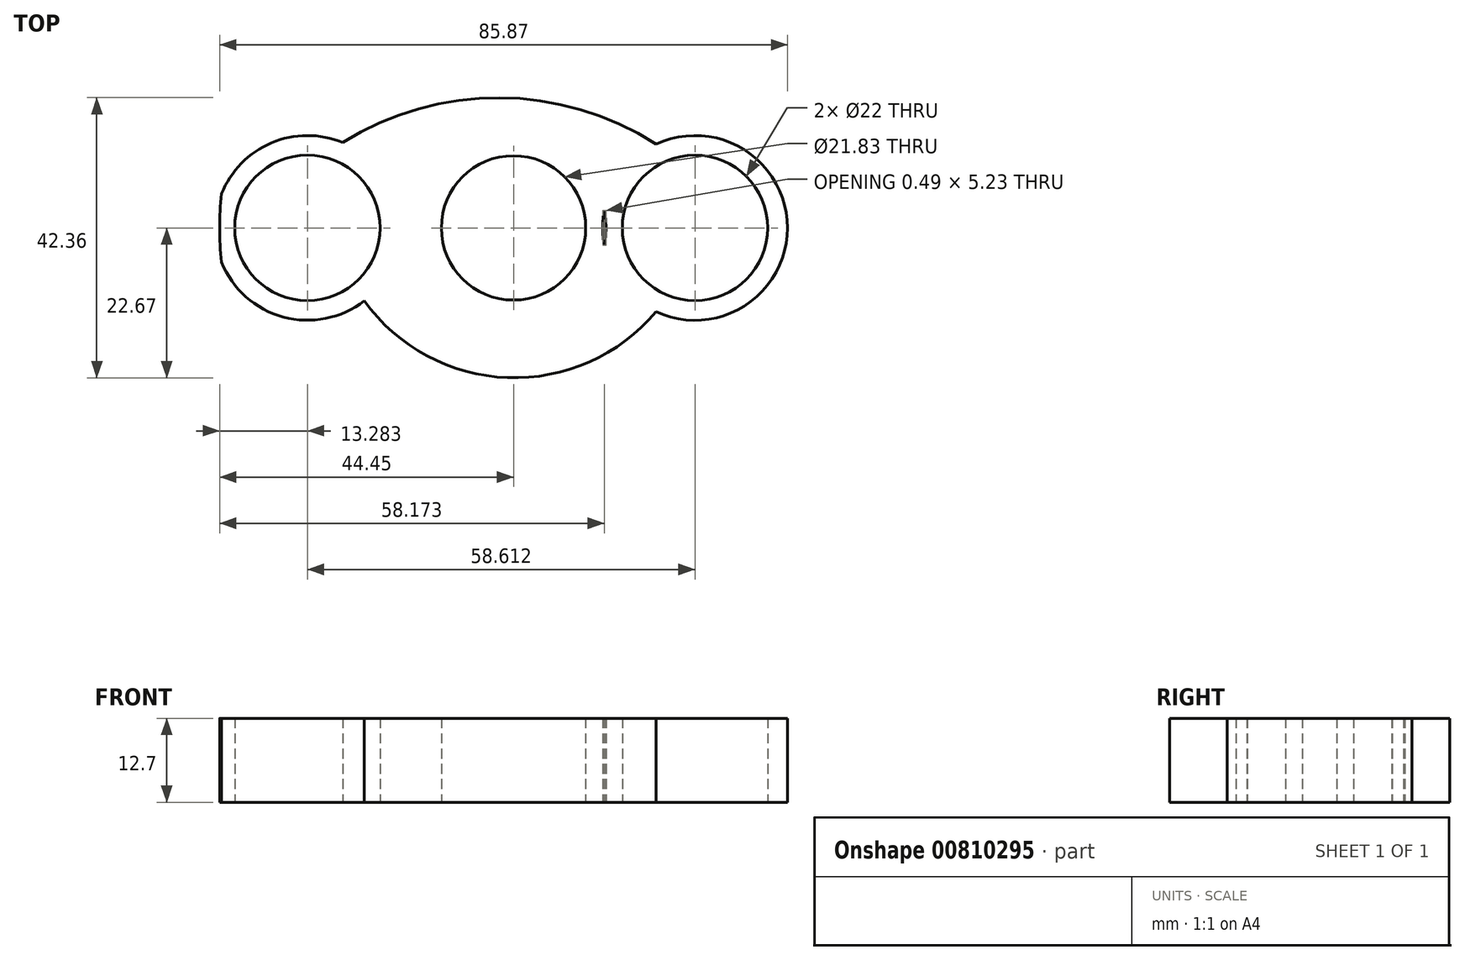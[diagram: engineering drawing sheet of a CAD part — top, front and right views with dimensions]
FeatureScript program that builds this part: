
annotation { "Feature Type Name" : "Feature", "Feature Type Description" : "" }
export const myFeature = defineFeature(function(context is Context, id is Id, definition is map)
    precondition{}
    {
        {
            var Q0;
            Q0=qCreatedBy(makeId("Top.planeOp"),FACE);
            var sketch = newSketch(context, id + "F0", { "sketchPlane" : qUnion([Q0])});
            skCircle(sketch, "E0", {"center": v(0, 0) * mm, "radius": 44.45 * mm});
            skCircle(sketch, "E1", {"center": v(0, 0) * mm, "radius": 10.91 * mm});
            skCircle(sketch, "E2", {"center": v(-31.17, 0) * mm, "radius": 11 * mm});
            skCircle(sketch, "E3", {"center": v(27.45, 0) * mm, "radius": 11 * mm});
            skCircle(sketch, "E4", {"center": v(-31.17, 0) * mm, "radius": 13.97 * mm});
            skCircle(sketch, "E5", {"center": v(0, 0) * mm, "radius": 13.97 * mm});
            skCircle(sketch, "E6", {"center": v(27.45, 0) * mm, "radius": 13.97 * mm});
            skArc(sketch, "E7", {"start": v(-22.58, -11.02) * mm, "mid": v(-0.92, -22.65) * mm, "end": v(21.55, -12.66) * mm});
            skArc(sketch, "E8", {"start": v(21.55, 12.66) * mm, "mid": v(-2.11, 19.69) * mm, "end": v(-25.84, 12.92) * mm});
            skSolve(sketch);
        }
        {
            var Q0;
            Q0=makeQuery(id+"F0.imprint","IMPRINT",FACE,{"disambiguationData":[TD([[makeQuery(id+"F0.imprint","IMPRINT",EDGE,{"derivedFrom":sQuery(id+"F0.wireOp",EDGE,"E2")}),-1.0]])]});
            var Q1;
            Q1=makeQuery(id+"F0.imprint","IMPRINT",FACE,{"disambiguationData":[TD([[makeQuery(id+"F0.imprint","IMPRINT",EDGE,{"derivedFrom":sQuery(id+"F0.wireOp",EDGE,"E1")}),-1.0]])]});
            var Q2;
            Q2=makeQuery(id+"F0.imprint","IMPRINT",FACE,{"disambiguationData":[TD([[makeQuery(id+"F0.imprint","IMPRINT",EDGE,{"derivedFrom":sQuery(id+"F0.wireOp",EDGE,"E3")}),-1.0]])]});
            var Q3;
            {var subQ5=sQuery(id+"F0.wireOp",EDGE,"E7");Q3=makeQuery(id+"F0.imprint","IMPRINT",FACE,{"disambiguationData":[TD([[makeQuery(id+"F0.imprint","IMPRINT",EDGE,{"derivedFrom":subQ5}),1.0]])]});}
            extrude(context, id + "F1", {"entities" : qUnion([Q0, Q1, Q2, Q3]), "depth" : 12.7 * mm, "offsetDistance" : 25.4 * mm});
        }
    });
